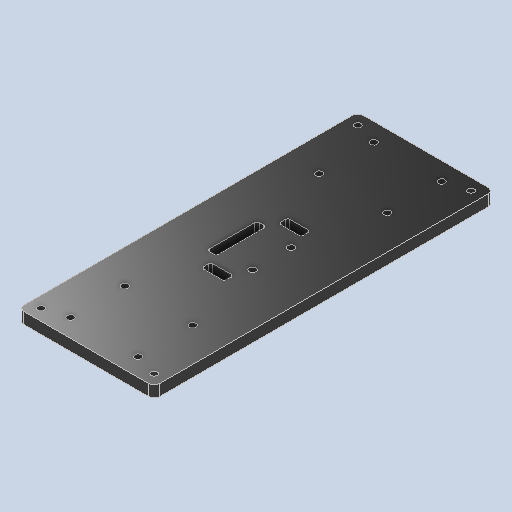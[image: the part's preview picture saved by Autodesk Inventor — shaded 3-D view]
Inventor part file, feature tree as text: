
AUTODESK INVENTOR PART (.ipt)
format: ipt  version: 2023 (Build 270158000, 158)  size: 362,496 bytes
history: native  units: in
note: dims shown in document units (in); Inventor stores cm internally (conversion verified against a paired STEP export)
features: fillet x4, extrude x2, sketch x1
ambient origin geometry x8: Origin, YZ Plane, XZ Plane, XY Plane, X Axis, Y Axis, Z Axis, Center Point
bodies: Solid1 (feature_tree)
feature tree (7):
  sketch  "Sketch1"  dims[d0=2.3622in d1=5.9055in d2=0.1969in d3=0.1969in d4=0.1969in d5=0.1969in d6=0.1969in d7=0.1969in d8=0.1969in d9=0.1969in d10=0.1102in d11=0.1102in d39=0.7492in d40=0.8681in d41=0.0984in d42=0.0984in d43=0.0984in d44=0.0984in d45=0.1181in d46=0.1181in d47=0.0394in d48=0.1575in d49=0.1969in d50=0.0in d51=0.0984in d52=0.0394in d53=0.0394in d54=0.7874in d55=1.5748in d56=0.7874in d57=0.7874in d58=1.5748in d59=0.7874in d60=0.315in d61=0.315in d62=0.1969in d63=1.1811in d64=0.9449in d65=0.9449in d66=0.1181in d67=0.1181in d68=0.1181in d69=0.1181in d70=0.1181in d71=0.1181in d72=0.1181in d73=0.1969in d74=0.0in d75=0.6299in d76=0.6299in d77=0.1969in d78=0.1575in d79=0.1969in d80=0.1969in d81=0.1575in d82=0.1969in d83=0.0394in]
  extrude  "Extrusion1"  Depth=5.9055in
  fillet  "Fillet1"  Radius=0.1969in
  fillet  "Fillet2"  Radius=0.1969in
  fillet  "Fillet3"  Radius=0.1969in
  extrude  "Extrusion2"  Depth=0.1969in
  fillet  "Fillet4"  Radius=0.1969in
